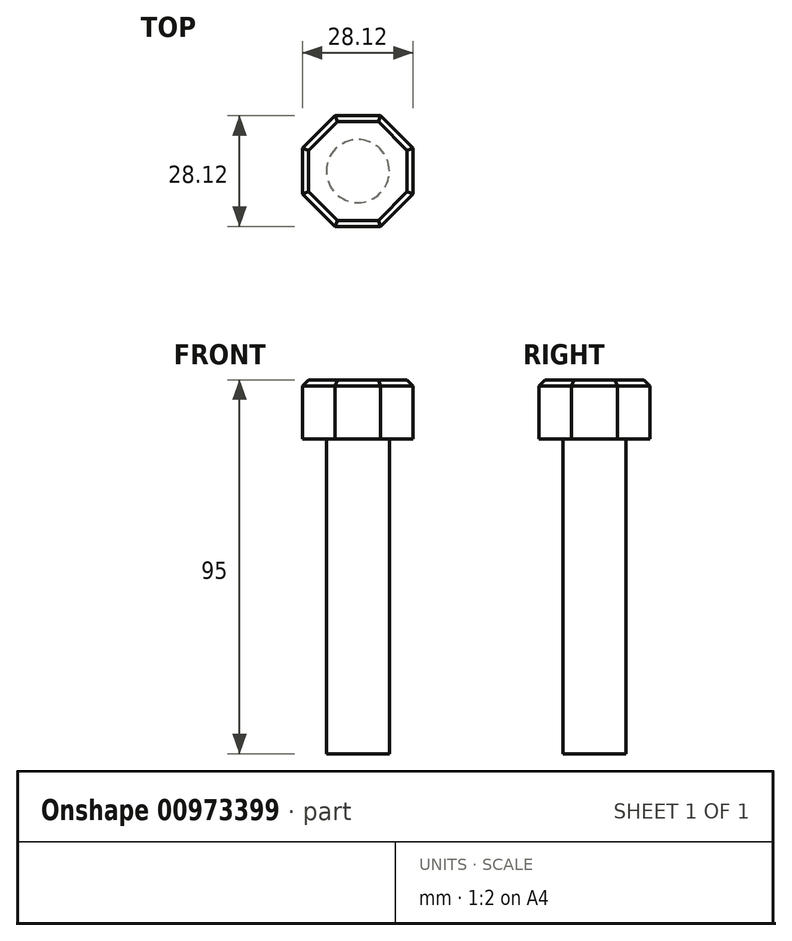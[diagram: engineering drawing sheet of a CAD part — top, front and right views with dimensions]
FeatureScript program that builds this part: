
annotation { "Feature Type Name" : "Feature", "Feature Type Description" : "" }
export const myFeature = defineFeature(function(context is Context, id is Id, definition is map)
    precondition{}
    {
        {
            var Q0;
            Q0=qCreatedBy(makeId("Top.planeOp"),FACE);
            var sketch = newSketch(context, id + "F0", { "sketchPlane" : qUnion([Q0])});
            skCircle(sketch, "E0", {"center": v(0, 0) * mm, "radius": 8 * mm});
            skSolve(sketch);
        }
        {
            var Q0;
            Q0=makeQuery(id+"F0.imprint","IMPRINT",FACE,{"disambiguationData":[TD([[makeQuery(id+"F0.imprint","IMPRINT",EDGE,{"derivedFrom":sQuery(id+"F0.wireOp",EDGE,"E0")}),1.0]])]});
            var sketch = newSketch(context, id + "F1", { "sketchPlane" : qUnion([Q0])});
            skCircle(sketch, "E1.cCircle", {"center": v(0, 0) * mm, "radius": 14.06 * mm, "construction": true});
            skLineSegment(sketch, "E1.0", {"start": v(14.06, 5.82) * mm, "end": v(14.06, -5.82) * mm});
            skLineSegment(sketch, "E1.1", {"start": v(14.06, -5.82) * mm, "end": v(5.82, -14.06) * mm});
            skLineSegment(sketch, "E1.2", {"start": v(5.82, -14.06) * mm, "end": v(-5.82, -14.06) * mm});
            skLineSegment(sketch, "E1.3", {"start": v(-5.82, -14.06) * mm, "end": v(-14.06, -5.82) * mm});
            skLineSegment(sketch, "E1.4", {"start": v(-14.06, -5.82) * mm, "end": v(-14.06, 5.82) * mm});
            skLineSegment(sketch, "E1.5", {"start": v(-14.06, 5.82) * mm, "end": v(-5.82, 14.06) * mm});
            skLineSegment(sketch, "E1.6", {"start": v(-5.82, 14.06) * mm, "end": v(5.82, 14.06) * mm});
            skLineSegment(sketch, "E1.7", {"start": v(5.82, 14.06) * mm, "end": v(14.06, 5.82) * mm});
            skPoint(sketch, "E1.0.midPoint", {"position": v(14.06, 0) * mm});
            skSolve(sketch);
        }
        {
            var Q0;
            Q0 = qSketchRegion(id + "F1", true);
            extrude(context, id + "F2", {"entities" : qUnion([Q0]), "depth" : 15 * mm, "offsetDistance" : 25 * mm});
        }
        {
            var Q0;
            Q0=makeQuery(id+"F0.imprint","IMPRINT",FACE,{"disambiguationData":[TD([[makeQuery(id+"F0.imprint","IMPRINT",EDGE,{"derivedFrom":sQuery(id+"F0.wireOp",EDGE,"E0")}),1.0]])]});
            extrude(context, id + "F3", {"entities" : qUnion([Q0]), "operationType" : NewBodyOperationType.ADD, "oppositeDirection" : true, "depth" : 80 * mm, "offsetDistance" : 25 * mm});
        }
        {
            var Q0;
            Q0=makeQuery(id+"F2.opExtrude","CAP_FACE",FACE,{"disambiguationData":[OSD([sQuery(id+"F1.wireOp",EDGE,"E1.0"),sQuery(id+"F1.wireOp",EDGE,"E1.1"),sQuery(id+"F1.wireOp",EDGE,"E1.2"),sQuery(id+"F1.wireOp",EDGE,"E1.3"),sQuery(id+"F1.wireOp",EDGE,"E1.4"),sQuery(id+"F1.wireOp",EDGE,"E1.5"),sQuery(id+"F1.wireOp",EDGE,"E1.6"),sQuery(id+"F1.wireOp",EDGE,"E1.7")])],"isStart":false});
            chamfer(context, id + "F4", {"entities" : qUnion([Q0]), "width" : 1.5 * mm, "tangentPropagation" : true});
        }
    });
